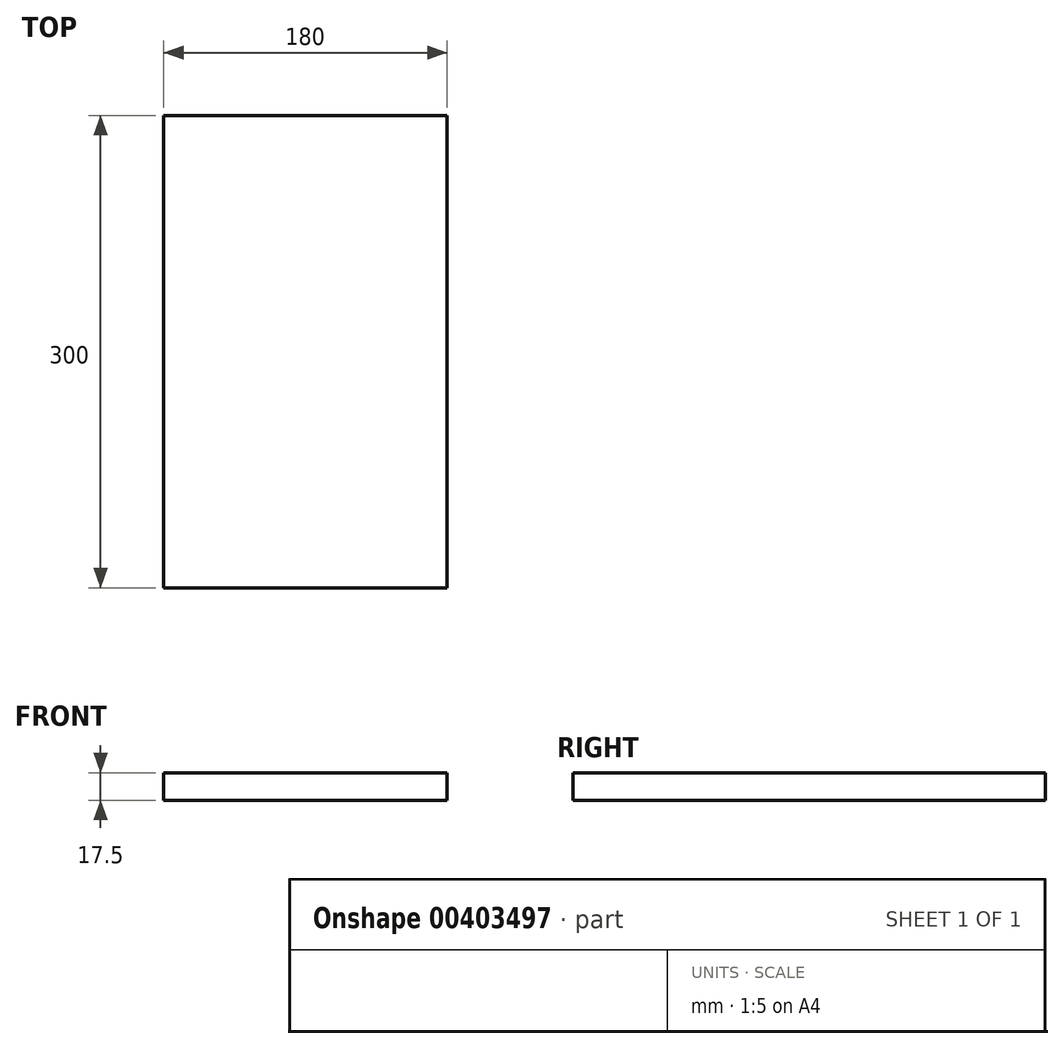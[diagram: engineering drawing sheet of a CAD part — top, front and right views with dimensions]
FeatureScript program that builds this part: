
annotation { "Feature Type Name" : "Feature", "Feature Type Description" : "" }
export const myFeature = defineFeature(function(context is Context, id is Id, definition is map)
    precondition{}
    {
        {
            var Q0;
            Q0=qCreatedBy(makeId("Top.planeOp"),FACE);
            var sketch = newSketch(context, id + "F0", { "sketchPlane" : qUnion([Q0])});
            skLineSegment(sketch, "E0.bottom", {"start": v(-127.73, 203.46) * mm, "end": v(52.27, 203.46) * mm});
            skLineSegment(sketch, "E0.top", {"start": v(-127.73, -96.54) * mm, "end": v(52.27, -96.54) * mm});
            skLineSegment(sketch, "E0.left", {"start": v(-127.73, 203.46) * mm, "end": v(-127.73, -96.54) * mm});
            skLineSegment(sketch, "E0.right", {"start": v(52.27, 203.46) * mm, "end": v(52.27, -96.54) * mm});
            skSolve(sketch);
        }
        {
            var Q0;
            Q0 = qSketchRegion(id + "F0", true);
            extrude(context, id + "F1", {"entities" : qUnion([Q0]), "oppositeDirection" : true, "depth" : 17.5 * mm});
        }
    });
